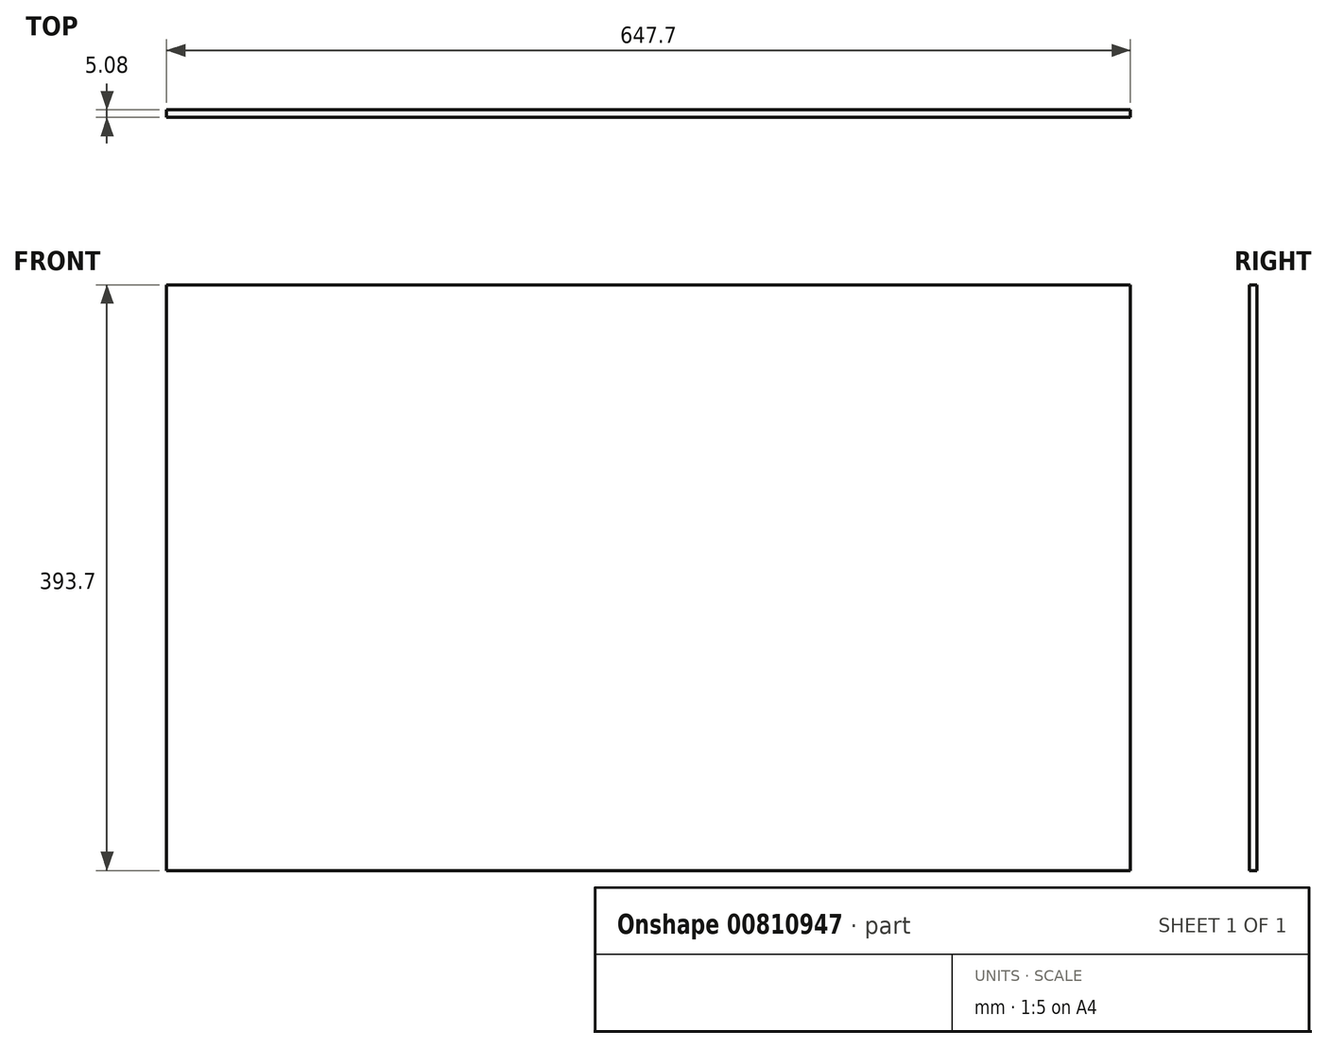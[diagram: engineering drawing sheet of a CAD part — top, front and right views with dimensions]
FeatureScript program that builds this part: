
annotation { "Feature Type Name" : "Feature", "Feature Type Description" : "" }
export const myFeature = defineFeature(function(context is Context, id is Id, definition is map)
    precondition{}
    {
        {
            var Q0;
            Q0=qCreatedBy(makeId("Front.planeOp"),FACE);
            var sketch = newSketch(context, id + "F0", { "sketchPlane" : qUnion([Q0])});
            skLineSegment(sketch, "E0.bottom", {"start": v(-323.2, 243.32) * mm, "end": v(324.5, 243.32) * mm});
            skLineSegment(sketch, "E0.top", {"start": v(-323.2, -150.38) * mm, "end": v(324.5, -150.38) * mm});
            skLineSegment(sketch, "E0.left", {"start": v(-323.2, 243.32) * mm, "end": v(-323.2, -150.38) * mm});
            skLineSegment(sketch, "E0.right", {"start": v(324.5, 243.32) * mm, "end": v(324.5, -150.38) * mm});
            skSolve(sketch);
        }
        {
            var Q0;
            Q0=makeQuery(id+"F0.imprint","IMPRINT",FACE,{"disambiguationData":[TD([[makeQuery(id+"F0.imprint","IMPRINT",EDGE,{"derivedFrom":sQuery(id+"F0.wireOp",EDGE,"E0.bottom")}),-1.0]])]});
            extrude(context, id + "F1", {"entities" : qUnion([Q0]), "depth" : 5.08 * mm, "offsetDistance" : 25.4 * mm});
        }
    });
